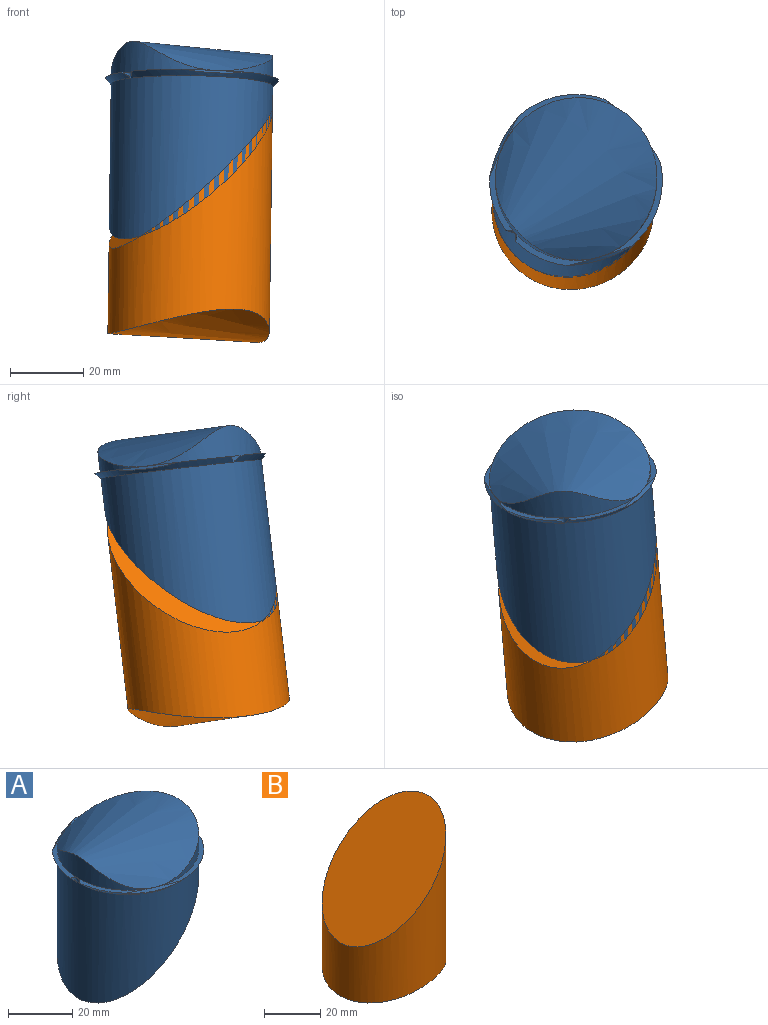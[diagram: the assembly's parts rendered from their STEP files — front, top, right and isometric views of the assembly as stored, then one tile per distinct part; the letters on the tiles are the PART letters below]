
ASSEMBLY  parts=2 mates=1
PART A: 12 faces, bbox 48.5x71.1x54.3 mm
  f0: cone r=6.94mm half-angle=46.2deg, axis (0.69,0,-0.72), area 13.7mm2, adj f1,f3
  f1: cone r=21.98mm half-angle=43.8deg, axis (0,0,1), area 127.2mm2, adj f0,f3,f6,f8,f11
  f2: cone r=21.98mm half-angle=43.8deg, axis (0,0,1), area 127.2mm2, adj f4,f6,f8,f10,f11
  f3: plane 45.42x23.53mm, normal (0,0,1), area 77.5mm2, adj f0,f1,f5,f8,f11
  f4: plane 45.42x23.53mm, normal (0,0,1), area 77.5mm2, adj f2,f5,f8,f10,f11
  f5: cylinder r=21.98mm len=43.96mm, axis (0,0,1), area 578.9mm2, adj f3,f4,f9
  f6: cylinder r=21.98mm len=44.29mm, axis (0,0,1), area 3164.2mm2, adj f1,f2,f7
  f7: plane 43.96x43.96mm, normal (0.69,0,-0.72), area 2103.6mm2, adj f6
  f8: cone r=6.94mm half-angle=43.8deg, axis (-0.69,0,0.72), area 4.5mm2, adj f1,f2,f3,f4
  f9: cone r=6.94mm half-angle=46.2deg, axis (0.69,0,-0.72), area 1629.9mm2, adj f5
  f10: cone r=6.94mm half-angle=46.2deg, axis (0.69,0,-0.72), area 13.7mm2, adj f2,f4
  f11: cone r=38.67mm half-angle=43.8deg, axis (-0.69,0,0.72), area 25.1mm2, adj f1,f2,f3,f4
PART B: 3 faces, bbox 47.1x66x65.4 mm
  f0: plane 43.96x43.96mm, normal (-0.69,0,0.72), area 2103.6mm2, adj f1
  f1: cylinder r=21.98mm len=65.38mm, axis (0,0,1), area 5711.8mm2, adj f0,f2
  f2: cone r=46.52mm half-angle=46.2deg, axis (-0.69,0,0.72), area 1571.5mm2, adj f1
PLACE A rot(axis=(-0.15,0.08,0.99),41.4deg) t=(43.07,-99.66,156.11)mm
PLACE B rot(axis=(-0.25,0.09,0.97),26.1deg) t=(43.04,-99.89,154.19)mm fixed
MATE cylindrical A.f1 <-> B.f1  axis (0.01,0.12,0.99) through (43.39,-96.82,180.37)mm
